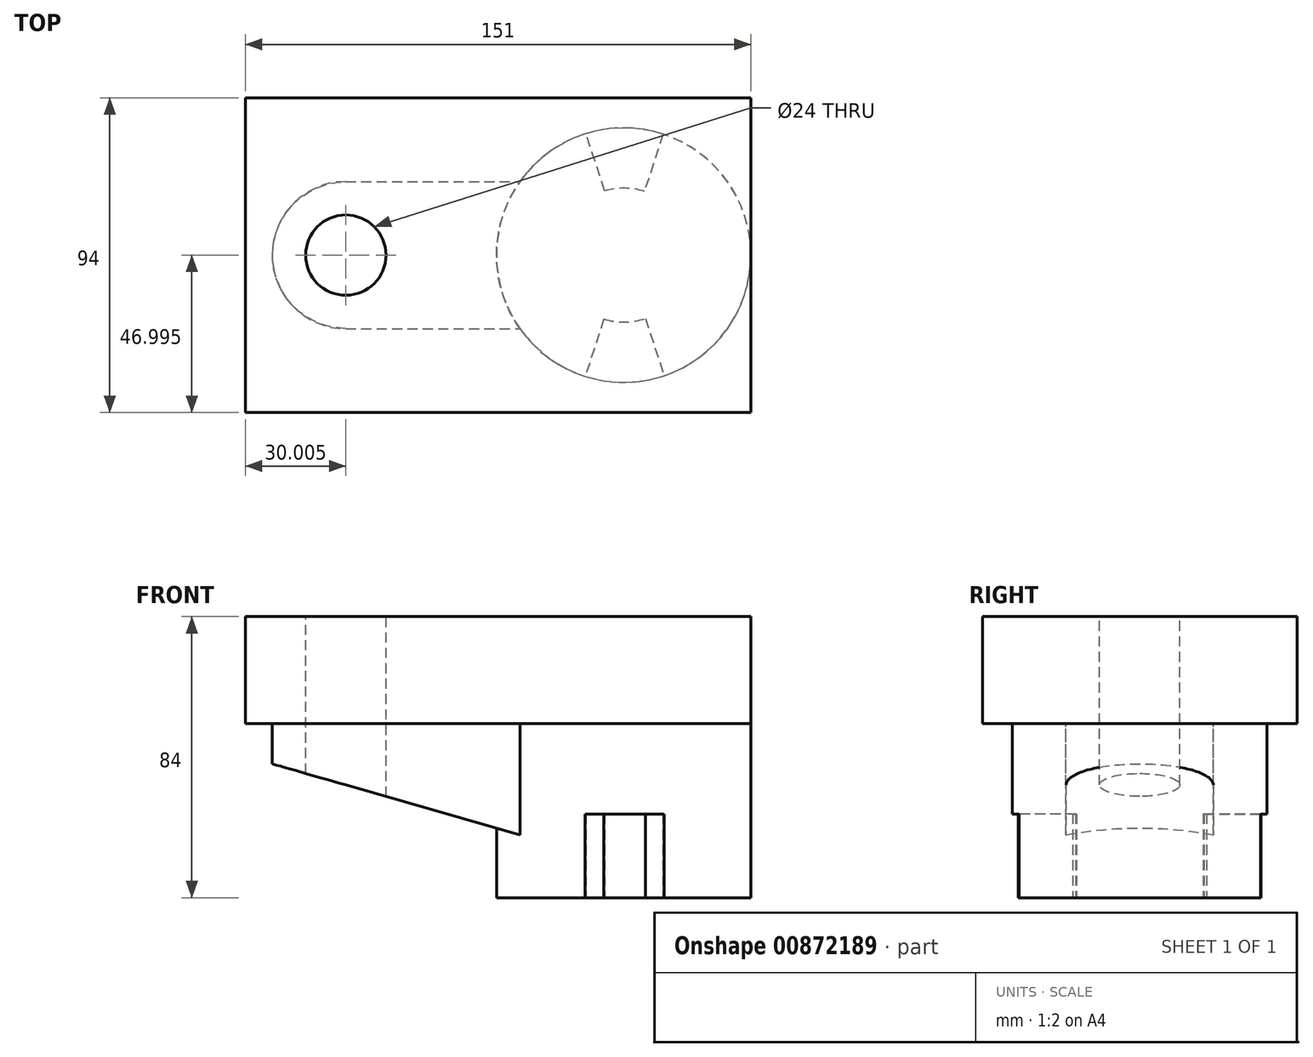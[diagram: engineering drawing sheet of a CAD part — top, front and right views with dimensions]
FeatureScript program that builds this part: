
annotation { "Feature Type Name" : "Feature", "Feature Type Description" : "" }
export const myFeature = defineFeature(function(context is Context, id is Id, definition is map)
    precondition{}
    {
        {
            var Q0;
            Q0=qCreatedBy(makeId("Top.planeOp"),FACE);
            var sketch = newSketch(context, id + "F0", { "sketchPlane" : qUnion([Q0])});
            skLineSegment(sketch, "E0", {"start": v(-77.65, 81.22) * mm, "end": v(-77.65, -12.78) * mm});
            skLineSegment(sketch, "E1", {"start": v(-77.65, -12.78) * mm, "end": v(-47.65, -12.78) * mm});
            skLineSegment(sketch, "E2", {"start": v(-47.65, -12.78) * mm, "end": v(35.35, -12.78) * mm});
            skLineSegment(sketch, "E3", {"start": v(35.35, 81.22) * mm, "end": v(-77.65, 81.22) * mm});
            skCircle(sketch, "E4", {"center": v(35.35, 34.22) * mm, "radius": 38 * mm});
            skLineSegment(sketch, "E5", {"start": v(73.35, 34.22) * mm, "end": v(73.35, 81.22) * mm});
            skLineSegment(sketch, "E6", {"start": v(73.35, 81.22) * mm, "end": v(35.35, 81.22) * mm});
            skLineSegment(sketch, "E7", {"start": v(35.35, -12.78) * mm, "end": v(73.35, -12.78) * mm});
            skLineSegment(sketch, "E8", {"start": v(73.35, -12.78) * mm, "end": v(73.35, 34.22) * mm});
            skCircle(sketch, "E9", {"center": v(-47.65, 34.22) * mm, "radius": 12 * mm});
            skCircle(sketch, "E10", {"center": v(-47.65, 34.22) * mm, "radius": 22 * mm});
            skLineSegment(sketch, "E11", {"start": v(-47.65, 56.22) * mm, "end": v(4.37, 56.22) * mm});
            skLineSegment(sketch, "E12", {"start": v(-47.65, 12.22) * mm, "end": v(4.37, 12.22) * mm});
            skLineSegment(sketch, "E13", {"start": v(35.35, 81.22) * mm, "end": v(35.35, -12.78) * mm});
            skPoint(sketch, "E14.orphan", {"position": v(-77.65, 34.22) * mm});
            skLineSegment(sketch, "E15.trimOffspring", {"start": v(-47.65, 56.22) * mm, "end": v(-47.65, 81.22) * mm});
            skArc(sketch, "E16", {"start": v(29.43, 15.11) * mm, "mid": v(35.67, 14.22) * mm, "end": v(41.87, 15.3) * mm});
            skLineSegment(sketch, "E17", {"start": v(41.87, 15.3) * mm, "end": v(47.43, -1.81) * mm});
            skLineSegment(sketch, "E18", {"start": v(29.43, 15.11) * mm, "end": v(23.87, -2) * mm});
            skLineSegment(sketch, "E19", {"start": v(29.67, 53.39) * mm, "end": v(24.1, 70.51) * mm});
            skLineSegment(sketch, "E20", {"start": v(47.11, 70.35) * mm, "end": v(41.55, 53.23) * mm});
            skLineSegment(sketch, "E21.trimOffspring", {"start": v(-2.65, 34.22) * mm, "end": v(-25.65, 34.22) * mm});
            skArc(sketch, "E22.trimOffspring", {"start": v(41.55, 53.23) * mm, "mid": v(35.62, 54.21) * mm, "end": v(29.67, 53.39) * mm});
            skSolve(sketch);
        }
        {
            var Q0;
            {var subQ4=sQuery(id+"F0.wireOp",EDGE,"E11");Q0=makeQuery(id+"F0.imprint","IMPRINT",FACE,{"disambiguationData":[TD([[makeQuery(id+"F0.imprint","IMPRINT",EDGE,{"derivedFrom":subQ4}),1.0]])]});}
            var Q1;
            {var subQ1=sQuery(id+"F0.wireOp",EDGE,"E0");Q1=makeQuery(id+"F0.imprint","IMPRINT",FACE,{"disambiguationData":[TD([[makeQuery(id+"F0.imprint","IMPRINT",EDGE,{"derivedFrom":subQ1}),1.0]])]});}
            var Q2;
            {var subQ0=sQuery(id+"F0.wireOp",EDGE,"E11");Q2=makeQuery(id+"F0.imprint","IMPRINT",FACE,{"disambiguationData":[TD([[makeQuery(id+"F0.imprint","IMPRINT",EDGE,{"derivedFrom":subQ0}),-1.0]])]});}
            var Q3;
            {var subQ0=sQuery(id+"F0.wireOp",EDGE,"E12");Q3=makeQuery(id+"F0.imprint","IMPRINT",FACE,{"disambiguationData":[TD([[makeQuery(id+"F0.imprint","IMPRINT",EDGE,{"derivedFrom":subQ0}),1.0]])]});}
            var Q4;
            Q4=makeQuery(id+"F0.imprint","IMPRINT",FACE,{"disambiguationData":[TD([[makeQuery(id+"F0.imprint","IMPRINT",EDGE,{"derivedFrom":sQuery(id+"F0.wireOp",EDGE,"E9")}),-1.0]])]});
            var Q5;
            Q5=makeQuery(id+"F0.imprint","IMPRINT",FACE,{"disambiguationData":[TD([[makeQuery(id+"F0.imprint","IMPRINT",EDGE,{"derivedFrom":sQuery(id+"F0.wireOp",EDGE,"E9")}),1.0]])]});
            var Q6;
            {var subQ2=sQuery(id+"F0.wireOp",EDGE,"E18");Q6=makeQuery(id+"F0.imprint","IMPRINT",FACE,{"disambiguationData":[TD([[makeQuery(id+"F0.imprint","IMPRINT",EDGE,{"derivedFrom":subQ2}),-1.0]])]});}
            var Q7;
            {var subQ0=sQuery(id+"F0.wireOp",EDGE,"E17");Q7=makeQuery(id+"F0.imprint","IMPRINT",FACE,{"disambiguationData":[TD([[makeQuery(id+"F0.imprint","IMPRINT",EDGE,{"derivedFrom":subQ0}),1.0]])]});}
            var Q8;
            {var subQ1=sQuery(id+"F0.wireOp",EDGE,"E5");Q8=makeQuery(id+"F0.imprint","IMPRINT",FACE,{"disambiguationData":[TD([[makeQuery(id+"F0.imprint","IMPRINT",EDGE,{"derivedFrom":subQ1}),1.0]])]});}
            var Q9;
            {var subQ0=sQuery(id+"F0.wireOp",EDGE,"E17");Q9=makeQuery(id+"F0.imprint","IMPRINT",FACE,{"disambiguationData":[TD([[makeQuery(id+"F0.imprint","IMPRINT",EDGE,{"derivedFrom":subQ0}),-1.0]])]});}
            var Q10;
            {var subQ0=sQuery(id+"F0.wireOp",EDGE,"E18");Q10=makeQuery(id+"F0.imprint","IMPRINT",FACE,{"disambiguationData":[TD([[makeQuery(id+"F0.imprint","IMPRINT",EDGE,{"derivedFrom":subQ0}),1.0]])]});}
            var Q11;
            {var subQ0=sQuery(id+"F0.wireOp",EDGE,"E19");Q11=makeQuery(id+"F0.imprint","IMPRINT",FACE,{"disambiguationData":[TD([[makeQuery(id+"F0.imprint","IMPRINT",EDGE,{"derivedFrom":subQ0}),-1.0]])]});}
            var Q12;
            {var subQ0=sQuery(id+"F0.wireOp",EDGE,"E20");Q12=makeQuery(id+"F0.imprint","IMPRINT",FACE,{"disambiguationData":[TD([[makeQuery(id+"F0.imprint","IMPRINT",EDGE,{"derivedFrom":subQ0}),-1.0]])]});}
            var Q13;
            {var subQ0=sQuery(id+"F0.wireOp",EDGE,"E7");Q13=makeQuery(id+"F0.imprint","IMPRINT",FACE,{"disambiguationData":[TD([[makeQuery(id+"F0.imprint","IMPRINT",EDGE,{"derivedFrom":subQ0}),1.0]])]});}
            extrude(context, id + "F1", {"entities" : qUnion([Q0, Q1, Q2, Q3, Q4, Q5, Q6, Q7, Q8, Q9, Q10, Q11, Q12, Q13]), "depth" : 32 * mm, "offsetDistance" : 25 * mm});
        }
        {
            var Q0;
            Q0=makeQuery(id+"F0.imprint","IMPRINT",FACE,{"disambiguationData":[TD([[makeQuery(id+"F0.imprint","IMPRINT",EDGE,{"derivedFrom":sQuery(id+"F0.wireOp",EDGE,"E9")}),-1.0]])]});
            var Q1;
            {var subQ0=sQuery(id+"F0.wireOp",EDGE,"E12");Q1=makeQuery(id+"F0.imprint","IMPRINT",FACE,{"disambiguationData":[TD([[makeQuery(id+"F0.imprint","IMPRINT",EDGE,{"derivedFrom":subQ0}),1.0]])]});}
            var Q2;
            {var subQ0=sQuery(id+"F0.wireOp",EDGE,"E11");Q2=makeQuery(id+"F0.imprint","IMPRINT",FACE,{"disambiguationData":[TD([[makeQuery(id+"F0.imprint","IMPRINT",EDGE,{"derivedFrom":subQ0}),-1.0]])]});}
            extrude(context, id + "F2", {"entities" : qUnion([Q0, Q1, Q2]), "operationType" : NewBodyOperationType.ADD, "oppositeDirection" : true, "depth" : 12 * mm, "offsetDistance" : 25 * mm});
        }
        {
            var Q0;
            {var subQ0=sQuery(id+"F0.wireOp",EDGE,"E17");Q0=makeQuery(id+"F0.imprint","IMPRINT",FACE,{"disambiguationData":[TD([[makeQuery(id+"F0.imprint","IMPRINT",EDGE,{"derivedFrom":subQ0}),1.0]])]});}
            var Q1;
            {var subQ2=sQuery(id+"F0.wireOp",EDGE,"E18");Q1=makeQuery(id+"F0.imprint","IMPRINT",FACE,{"disambiguationData":[TD([[makeQuery(id+"F0.imprint","IMPRINT",EDGE,{"derivedFrom":subQ2}),-1.0]])]});}
            extrude(context, id + "F3", {"entities" : qUnion([Q0, Q1]), "operationType" : NewBodyOperationType.ADD, "oppositeDirection" : true, "depth" : 52 * mm, "offsetDistance" : 25 * mm});
        }
        {
            var Q0;
            Q0=makeQuery(id+"F2.opExtrude","SWEPT_FACE",FACE,{"disambiguationData":[OSD([sQuery(id+"F0.wireOp",EDGE,"E12")])]});
            var sketch = newSketch(context, id + "F4", { "sketchPlane" : qUnion([Q0])});
            skLineSegment(sketch, "E23.0", {"start": v(-69.65, 0) * mm, "end": v(-25.65, 0) * mm});
            skLineSegment(sketch, "E24.0.0", {"start": v(4.37, 0) * mm, "end": v(-47.65, 0) * mm});
            skLineSegment(sketch, "E24.0.1", {"start": v(-47.65, 0) * mm, "end": v(-47.65, -12) * mm});
            skLineSegment(sketch, "E24.0.2", {"start": v(-47.65, -12) * mm, "end": v(4.37, -12) * mm});
            skLineSegment(sketch, "E24.0.3", {"start": v(4.37, -12) * mm, "end": v(4.37, 0) * mm});
            skLineSegment(sketch, "E25.0", {"start": v(-59.65, 0) * mm, "end": v(-35.65, 0) * mm});
            skLineSegment(sketch, "E26", {"start": v(-69.65, -12) * mm, "end": v(-69.65, 0) * mm});
            skLineSegment(sketch, "E27.0", {"start": v(-47.65, -12) * mm, "end": v(-69.65, -12) * mm});
            skLineSegment(sketch, "E28", {"start": v(-69.65, -12) * mm, "end": v(4.37, -33.22) * mm});
            skLineSegment(sketch, "E29", {"start": v(4.37, -33.22) * mm, "end": v(4.37, -12) * mm});
            skSolve(sketch);
        }
        {
            var Q0;
            Q0 = qSketchRegion(id + "FnVqHTBIgg7MZUW_1", true);
            var Q1;
            Q1=makeQuery(id+"F4.imprint","IMPRINT",FACE,{"disambiguationData":[TD([[makeQuery(id+"F4.imprint","IMPRINT",EDGE,{"derivedFrom":sQuery(id+"F4.wireOp",EDGE,"E24.0.2")}),-1.0]])]});
            extrude(context, id + "F5", {"entities" : qUnion([Q0, Q1]), "operationType" : NewBodyOperationType.ADD, "oppositeDirection" : true, "depth" : 44 * mm, "offsetDistance" : 25 * mm});
        }
        {
            var Q0;
            {var subQ1=sQuery(id+"F4.wireOp",EDGE,"E27.0");var subQ2=sQuery(id+"F4.wireOp",EDGE,"E24.0.2");var subQ3=makeQuery(id+"F5.opExtrude","SWEPT_FACE",FACE,{"disambiguationData":[OSD([subQ2,subQ1])]});Q0=makeQuery(id+"F5.boolean.opBoolean","SPLIT",FACE,{"disambiguationData":[TD([makeQuery(id+"F2.opExtrude","SWEPT_FACE",FACE,{"disambiguationData":[OSD([sQuery(id+"F0.wireOp",EDGE,"E11")])]})])],"derivedFrom":subQ3});}
            var Q1;
            {var subQ1=sQuery(id+"F4.wireOp",EDGE,"E27.0");var subQ2=sQuery(id+"F4.wireOp",EDGE,"E24.0.2");var subQ3=makeQuery(id+"F5.opExtrude","SWEPT_FACE",FACE,{"disambiguationData":[OSD([subQ2,subQ1])]});Q1=makeQuery(id+"F5.boolean.opBoolean","SPLIT",FACE,{"disambiguationData":[TD([makeQuery(id+"F2.opExtrude","SWEPT_FACE",FACE,{"disambiguationData":[OSD([sQuery(id+"F0.wireOp",EDGE,"E12")])]})])],"derivedFrom":subQ3});}
            extrude(context, id + "F6", {"entities" : qUnion([Q0, Q1]), "operationType" : NewBodyOperationType.REMOVE, "oppositeDirection" : true, "depth" : 93.7 * mm, "offsetDistance" : 25 * mm});
        }
        {
            var Q0;
            Q0=makeQuery(id+"F1.opExtrude","CAP_FACE",FACE,{"disambiguationData":[OSD([sQuery(id+"F0.wireOp",EDGE,"E0"),sQuery(id+"F0.wireOp",EDGE,"E1"),sQuery(id+"F0.wireOp",EDGE,"E2"),sQuery(id+"F0.wireOp",EDGE,"E3"),sQuery(id+"F0.wireOp",EDGE,"E5"),sQuery(id+"F0.wireOp",EDGE,"E6"),sQuery(id+"F0.wireOp",EDGE,"E7"),sQuery(id+"F0.wireOp",EDGE,"E8")])],"isStart":false});
            var sketch = newSketch(context, id + "F7", { "sketchPlane" : qUnion([Q0])});
            skCircle(sketch, "E30.0", {"center": v(-47.65, 34.22) * mm, "radius": 12 * mm});
            skSolve(sketch);
        }
        {
            var Q0;
            Q0 = qSketchRegion(id + "F7", true);
            extrude(context, id + "F8", {"entities" : qUnion([Q0]), "operationType" : NewBodyOperationType.REMOVE, "oppositeDirection" : true, "depth" : 98.4 * mm, "offsetDistance" : 25 * mm});
        }
        {
            var Q0;
            {var subQ0=sQuery(id+"F0.wireOp",EDGE,"E20");Q0=makeQuery(id+"F0.imprint","IMPRINT",FACE,{"disambiguationData":[TD([[makeQuery(id+"F0.imprint","IMPRINT",EDGE,{"derivedFrom":subQ0}),-1.0]])]});}
            var Q1;
            {var subQ0=sQuery(id+"F0.wireOp",EDGE,"E19");Q1=makeQuery(id+"F0.imprint","IMPRINT",FACE,{"disambiguationData":[TD([[makeQuery(id+"F0.imprint","IMPRINT",EDGE,{"derivedFrom":subQ0}),-1.0]])]});}
            var Q2;
            {var subQ0=sQuery(id+"F0.wireOp",EDGE,"E17");Q2=makeQuery(id+"F0.imprint","IMPRINT",FACE,{"disambiguationData":[TD([[makeQuery(id+"F0.imprint","IMPRINT",EDGE,{"derivedFrom":subQ0}),-1.0]])]});}
            var Q3;
            {var subQ0=sQuery(id+"F0.wireOp",EDGE,"E18");Q3=makeQuery(id+"F0.imprint","IMPRINT",FACE,{"disambiguationData":[TD([[makeQuery(id+"F0.imprint","IMPRINT",EDGE,{"derivedFrom":subQ0}),1.0]])]});}
            extrude(context, id + "F9", {"entities" : qUnion([Q0, Q1, Q2, Q3]), "operationType" : NewBodyOperationType.ADD, "oppositeDirection" : true, "depth" : 52 * mm, "offsetDistance" : 25 * mm});
        }
        {
            var Q0;
            {var subQ0=sQuery(id+"F0.wireOp",EDGE,"E18");var subQ1=sQuery(id+"F0.wireOp",EDGE,"E17");var subQ2=sQuery(id+"F0.wireOp",EDGE,"E16");var subQ3=sQuery(id+"F0.wireOp",EDGE,"E4");var subQ4=sQuery(id+"F0.wireOp",EDGE,"E22.trimOffspring");var subQ5=sQuery(id+"F0.wireOp",EDGE,"E20");var subQ6=sQuery(id+"F0.wireOp",EDGE,"E19");Q0=makeQuery(id+"F9.boolean.opBoolean","MERGE",FACE,{"derivedFrom":[makeQuery(id+"F3.opExtrude","CAP_FACE",FACE,{"disambiguationData":[OSD([subQ3,subQ2,subQ1,subQ0,subQ6,subQ5,subQ4])],"isStart":false}),makeQuery(id+"F9.opExtrude","CAP_FACE",FACE,{"disambiguationData":[OSD([subQ3,subQ6,subQ5,subQ4])],"isStart":false}),makeQuery(id+"F9.opExtrude","CAP_FACE",FACE,{"disambiguationData":[OSD([subQ3,subQ2,subQ1,subQ0])],"isStart":false})]});}
            var sketch = newSketch(context, id + "F10", { "sketchPlane" : qUnion([Q0])});
            skLineSegment(sketch, "E31.0", {"start": v(41.87, -15.3) * mm, "end": v(47.43, 1.81) * mm});
            skLineSegment(sketch, "E32.0", {"start": v(29.43, -15.11) * mm, "end": v(23.87, 2) * mm});
            skArc(sketch, "E33.0", {"start": v(29.43, -15.11) * mm, "mid": v(35.67, -14.22) * mm, "end": v(41.87, -15.3) * mm});
            skCircle(sketch, "E34.0", {"center": v(35.35, -34.22) * mm, "radius": 38 * mm});
            skLineSegment(sketch, "E35.0", {"start": v(47.11, -70.35) * mm, "end": v(41.55, -53.23) * mm});
            skPoint(sketch, "E36.0", {"position": v(35.62, -54.21) * mm});
            skArc(sketch, "E37.0", {"start": v(41.55, -53.23) * mm, "mid": v(35.62, -54.21) * mm, "end": v(29.67, -53.39) * mm});
            skPoint(sketch, "E38.0", {"position": v(26.88, -61.95) * mm});
            skLineSegment(sketch, "E39.0", {"start": v(29.67, -53.39) * mm, "end": v(24.1, -70.51) * mm});
            skSolve(sketch);
        }
        {
            var Q0;
            {var subQ0=sQuery(id+"F10.wireOp",EDGE,"E35.0");Q0=makeQuery(id+"F10.imprint","IMPRINT",FACE,{"disambiguationData":[TD([[makeQuery(id+"F10.imprint","IMPRINT",EDGE,{"derivedFrom":subQ0}),1.0]])]});}
            var Q1;
            {var subQ0=sQuery(id+"F10.wireOp",EDGE,"E31.0");Q1=makeQuery(id+"F10.imprint","IMPRINT",FACE,{"disambiguationData":[TD([[makeQuery(id+"F10.imprint","IMPRINT",EDGE,{"derivedFrom":subQ0}),1.0]])]});}
            extrude(context, id + "F11", {"entities" : qUnion([Q0, Q1]), "operationType" : NewBodyOperationType.REMOVE, "oppositeDirection" : true, "depth" : 25 * mm, "offsetDistance" : 25 * mm});
        }
    });
